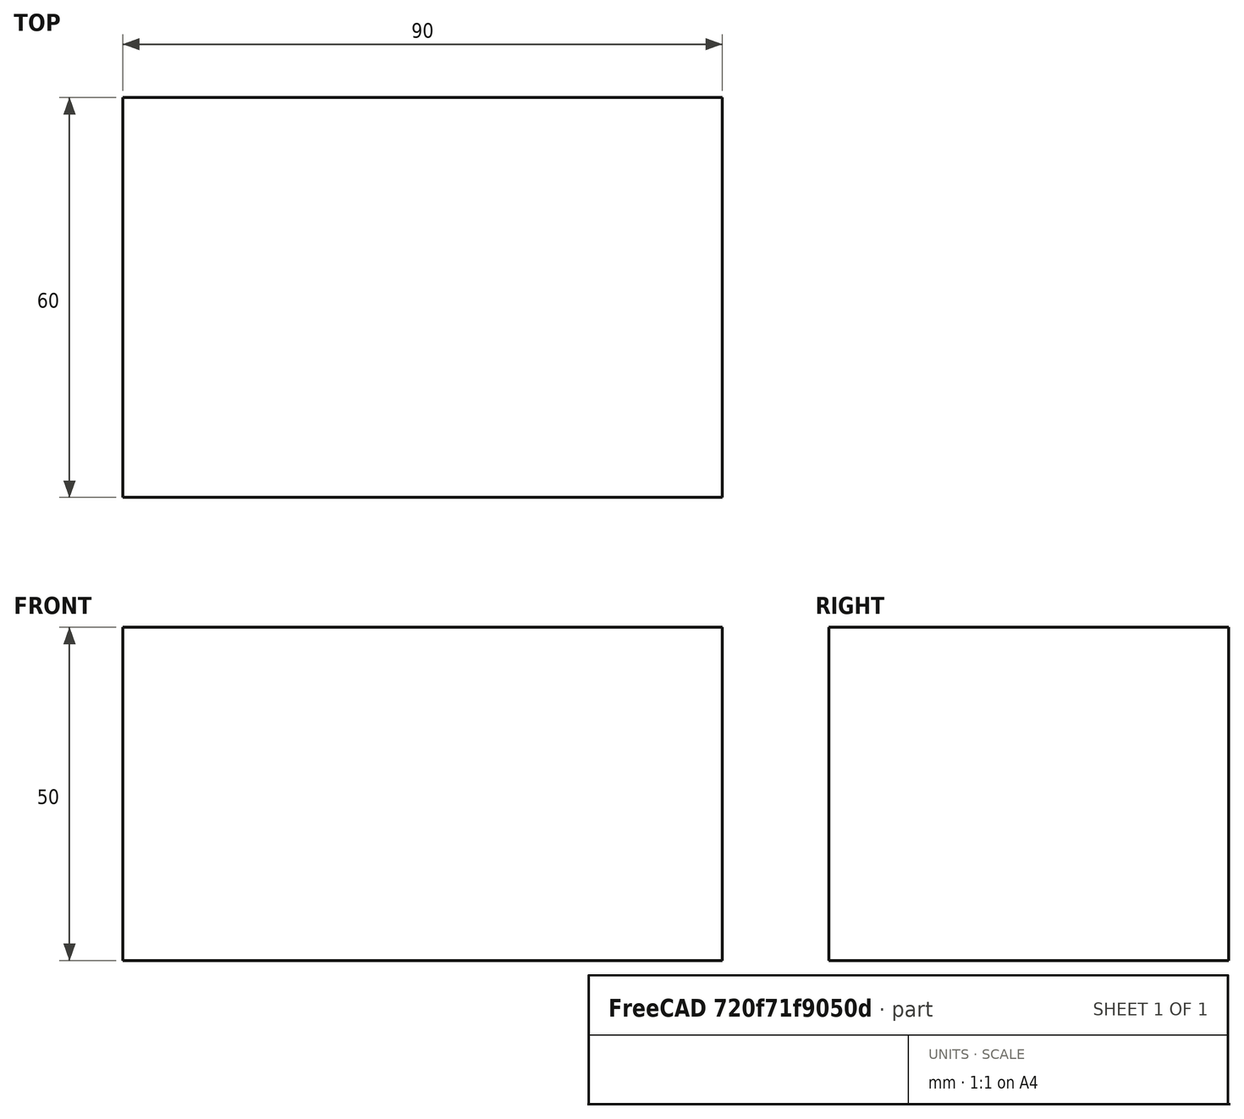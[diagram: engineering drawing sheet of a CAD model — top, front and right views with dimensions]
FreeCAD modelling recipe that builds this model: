
FCSTD DOCUMENT  (FreeCAD 0.15R4671 (Git))
Label: Flat Bar 90x60 EN10058 S235JR
License: All rights reserved
LicenseURL: http://en.wikipedia.org/wiki/All_rights_reserved
objects: Sketcher::SketchObject×1, Part::Extrusion×1
note: 2 computed .brp shape members not serialized (recipe doc carries the construction recipe); baked Part::Feature solids carry a one-line shape summary decoded from their .brp

FEATURE [Sketcher::SketchObject] Sketch
  sketch-geometry (4):
    g0: LineSegment StartX=-45 StartY=-30 StartZ=0 EndX=45 EndY=-30 EndZ=0
    g1: LineSegment StartX=45 StartY=-30 StartZ=0 EndX=45 EndY=30 EndZ=0
    g2: LineSegment StartX=45 StartY=30 StartZ=0 EndX=-45 EndY=30 EndZ=0
    g3: LineSegment StartX=-45 StartY=30 StartZ=0 EndX=-45 EndY=-30 EndZ=0
  constraints (12):
    c: Coincident(g0,g1)
    c: Coincident(g1,g2)
    c: Coincident(g2,g3)
    c: Coincident(g3,g0)
    c: Horizontal(g0)
    c: Horizontal(g2)
    c: Vertical(g1)
    c: Vertical(g3)
    c: Symmetric(g1,g2,g-2)
    c: Symmetric(g0,g1,g-1)
    c: DistanceY(g1) = 60
    c: DistanceX(g0) = 90
FEATURE [Part::Extrusion] Extrude  label="Flat Bar 90x60 EN10058 S235JR"
  Base = -> Sketch
  Dir = (0,0,50)
  Solid = true
